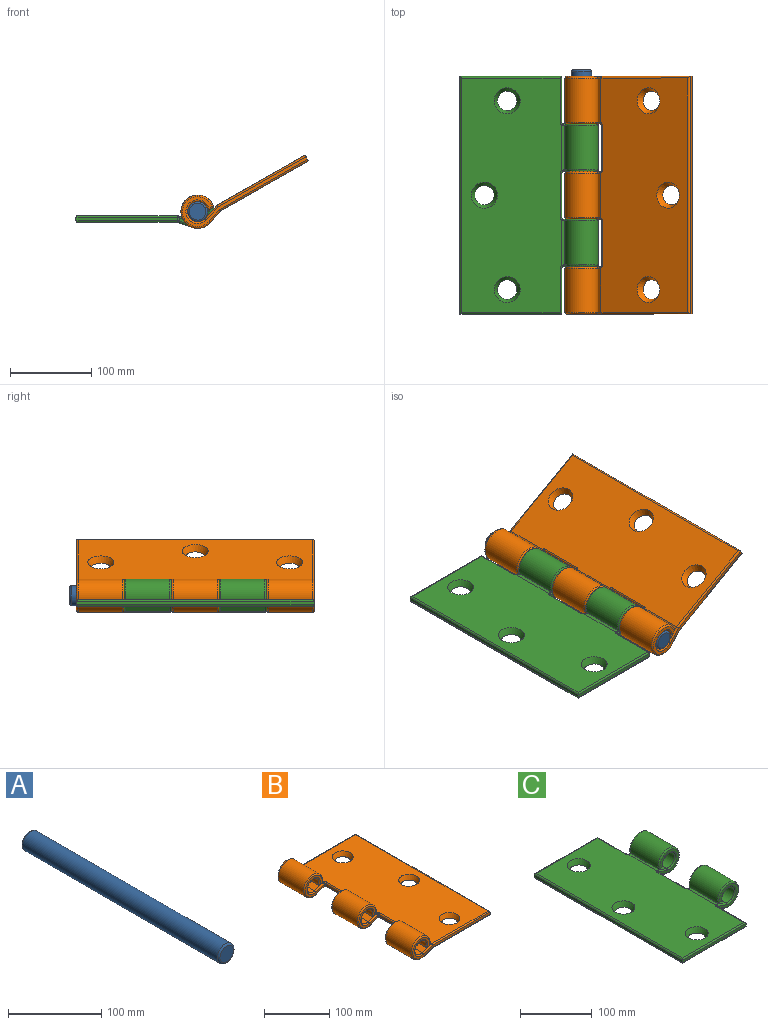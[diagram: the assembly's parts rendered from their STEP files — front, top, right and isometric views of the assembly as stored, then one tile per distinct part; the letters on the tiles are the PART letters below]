
ASSEMBLY  parts=3 mates=2
PART A: 5 faces, bbox 26.5x300x26.5 mm
  f0: cylinder r=12.25mm len=296mm, axis (0,-1,0), area 22782.8mm2, adj f3,f4
  f1: plane 20.5x20.5mm, normal (0,1,0), area 330.1mm2, adj f4
  f2: plane 20.5x20.5mm, normal (0,-1,0), area 330.1mm2, adj f3
  f3: torus R=10.25mm, axis (0,-1,0), area 227.5mm2, adj f0,f2
  f4: torus R=10.25mm, axis (0,-1,0), area 227.5mm2, adj f0,f1
PART B: 89 faces, bbox 171.7x292x44.4 mm
  f0: plane 55.3x20.54mm, normal (-0.32,0,0.95), area 1179mm2, adj f8,f11,f42,f44,f46,f80
  f1: plane 56.21x20.54mm, normal (-0.32,0,0.95), area 1179.8mm2, adj f9,f11,f50,f51,f52,f62,f64,f66
  f2: plane 54.63x17.59mm, normal (0.34,0,-0.94), area 1016.4mm2, adj f4,f13,f33,f34,f73
  f3: plane 54.85x17.59mm, normal (0.34,0,-0.94), area 1016.5mm2, adj f5,f13,f41,f43,f53,f54
  f4: cylinder r=20.5mm len=54.4mm, axis (0,1,0), area 5913.6mm2, adj f2,f6,f36,f74
  f5: cylinder r=20.5mm len=54.4mm, axis (0,1,0), area 5913.6mm2, adj f3,f7,f45,f56
  f6: plane 54.4x8.42mm, normal (0,0,-1), area 458.3mm2, adj f4,f8,f38,f76
  f7: plane 54.4x8.42mm, normal (0,0,-1), area 458.3mm2, adj f5,f9,f47,f58
  f8: cylinder r=12.5mm len=54.4mm, axis (0,1,0), area 3703.3mm2, adj f0,f6,f40,f78
  f9: cylinder r=12.5mm len=54.4mm, axis (0,1,0), area 3703.3mm2, adj f1,f7,f49,f60
  f10: plane 55.3x20.54mm, normal (-0.32,0,0.95), area 1179mm2, adj f11,f17,f70,f71,f72,f88
  f11: plane 288x123mm, normal (0,0,1), area 32774mm2, adj f0,f1,f10,f20,f21,f22,f46,f48
  f12: plane 292x4mm, normal (1,0,0), area 1168mm2, adj f18,f19,f77,f84
  f13: plane 288x123.06mm, normal (0,0,-1), area 33829.6mm2, adj f2,f3,f14,f20,f21,f22,f33,f35
  f14: plane 54.63x17.59mm, normal (0.34,0,-0.94), area 1016.4mm2, adj f13,f15,f61,f63,f81
  f15: cylinder r=20.5mm len=54.4mm, axis (0,1,0), area 5913.6mm2, adj f14,f16,f65,f83
  f16: plane 54.4x8.42mm, normal (0,0,-1), area 458.3mm2, adj f15,f17,f67,f85
  f17: cylinder r=12.5mm len=54.4mm, axis (0,1,0), area 3703.3mm2, adj f10,f16,f69,f87
  f18: plane 168x37mm, normal (0,-1,0), area 921.5mm2, adj f12,f79,f81,f83,f85,f86,f87,f88
  f19: plane 168x37mm, normal (0,1,0), area 921.5mm2, adj f12,f73,f74,f75,f76,f78,f80,f82
  f20: cone r=12mm half-angle=26.6deg, axis (0,0,1), area 786.8mm2, adj f11,f13
  f21: cone r=12mm half-angle=26.6deg, axis (0,0,1), area 786.8mm2, adj f11,f13
  f22: cone r=12mm half-angle=26.6deg, axis (0,0,1), area 786.8mm2, adj f11,f13
  f23: plane 54.4x4mm, normal (-1,0,0), area 217.6mm2, adj f29,f30,f57,f68
  f24: plane 41x37mm, normal (0,1,0), area 413.9mm2, adj f29,f63,f65,f67,f69,f71
  f25: plane 41x37mm, normal (0,-1,0), area 413.9mm2, adj f30,f54,f56,f58,f60,f62
  f26: plane 54.4x4mm, normal (-1,0,0), area 217.6mm2, adj f31,f32,f37,f48
  f27: plane 41x37mm, normal (0,1,0), area 413.9mm2, adj f31,f43,f45,f47,f49,f51
  f28: plane 41x37mm, normal (0,-1,0), area 413.9mm2, adj f32,f34,f36,f38,f40,f42
  f29: cylinder r=2mm len=4.59mm, axis (0,0,-1), area 12.3mm2, adj f23,f24,f59,f61,f70,f72
  f30: cylinder r=2mm len=4.59mm, axis (0,0,1), area 12.3mm2, adj f23,f25,f53,f55,f64,f66
  f31: cylinder r=2mm len=4.59mm, axis (0,0,-1), area 12.3mm2, adj f26,f27,f39,f41,f50,f52
  f32: cylinder r=2mm len=4.59mm, axis (0,0,1), area 12.3mm2, adj f26,f28,f33,f35,f44,f46
  f33: bspline ~2.47x2.33mm, area 3.5mm2, adj f2,f13,f32,f34,f35
  f34: cylinder r=2mm len=16.94mm, axis (-0.94,0,-0.34), area 54.3mm2, adj f2,f28,f33,f36
  f35: torus R=4mm, axis (0,0,-1), area 9.2mm2, adj f13,f32,f33,f37
  f36: torus R=18.5mm, axis (0,-1,0), area 326.9mm2, adj f4,f28,f34,f38
  f37: cylinder r=2mm len=54.4mm, axis (0,1,0), area 170.9mm2, adj f13,f26,f35,f39
  f38: cylinder r=2mm len=8.42mm, axis (-1,0,0), area 19.6mm2, adj f6,f28,f36,f40
  f39: torus R=4mm, axis (0,0,-1), area 9.2mm2, adj f13,f31,f37,f41
  f40: torus R=14.5mm, axis (0,-1,0), area 222mm2, adj f8,f28,f38,f42
  f41: bspline ~2.47x2.33mm, area 3.5mm2, adj f3,f13,f31,f39,f43
  f42: cylinder r=2mm len=18.54mm, axis (0.95,0,0.32), area 59.3mm2, adj f0,f28,f40,f44
  f43: cylinder r=2mm len=16.94mm, axis (0.94,0,0.34), area 54.3mm2, adj f3,f27,f41,f45
  f44: bspline ~2.75x2.54mm, area 6mm2, adj f0,f32,f42,f46
  f45: torus R=18.5mm, axis (0,-1,0), area 326.9mm2, adj f5,f27,f43,f47
  f46: torus R=4mm, axis (0,0,-1), area 8.7mm2, adj f0,f11,f32,f44,f48
  f47: cylinder r=2mm len=8.42mm, axis (1,0,0), area 19.6mm2, adj f7,f27,f45,f49
  f48: cylinder r=2mm len=54.4mm, axis (0,-1,0), area 170.9mm2, adj f11,f26,f46,f50
  f49: torus R=14.5mm, axis (0,-1,0), area 222mm2, adj f9,f27,f47,f51
  f50: torus R=4mm, axis (0,0,-1), area 8.7mm2, adj f1,f11,f31,f48,f52
  f51: cylinder r=2mm len=18.54mm, axis (-0.95,0,-0.32), area 59.3mm2, adj f1,f27,f49,f52
  f52: bspline ~2.75x2.54mm, area 6mm2, adj f1,f31,f50,f51
  f53: bspline ~2.47x2.33mm, area 3.5mm2, adj f3,f13,f30,f54,f55
  f54: cylinder r=2mm len=16.94mm, axis (-0.94,0,-0.34), area 54.3mm2, adj f3,f25,f53,f56
  f55: torus R=4mm, axis (0,0,-1), area 9.2mm2, adj f13,f30,f53,f57
  f56: torus R=18.5mm, axis (0,-1,0), area 326.9mm2, adj f5,f25,f54,f58
  f57: cylinder r=2mm len=54.4mm, axis (0,1,0), area 170.9mm2, adj f13,f23,f55,f59
  f58: cylinder r=2mm len=8.42mm, axis (-1,0,0), area 19.6mm2, adj f7,f25,f56,f60
  f59: torus R=4mm, axis (0,0,-1), area 9.2mm2, adj f13,f29,f57,f61
  f60: torus R=14.5mm, axis (0,-1,0), area 222mm2, adj f9,f25,f58,f62
  f61: bspline ~2.47x2.33mm, area 3.5mm2, adj f13,f14,f29,f59,f63
  f62: cylinder r=2mm len=18.54mm, axis (0.95,0,0.32), area 59.3mm2, adj f1,f25,f60,f64
  f63: cylinder r=2mm len=16.94mm, axis (0.94,0,0.34), area 54.3mm2, adj f14,f24,f61,f65
  f64: bspline ~3.65x3.11mm, area 6mm2, adj f1,f30,f62,f66
  f65: torus R=18.5mm, axis (0,-1,0), area 326.9mm2, adj f15,f24,f63,f67
  f66: torus R=4mm, axis (0,0,-1), area 8.7mm2, adj f1,f11,f30,f64,f68
  f67: cylinder r=2mm len=8.42mm, axis (1,0,0), area 19.6mm2, adj f16,f24,f65,f69
  f68: cylinder r=2mm len=54.4mm, axis (0,-1,0), area 170.9mm2, adj f11,f23,f66,f70
  f69: torus R=14.5mm, axis (0,-1,0), area 222mm2, adj f17,f24,f67,f71
  f70: torus R=4mm, axis (0,0,-1), area 8.7mm2, adj f10,f11,f29,f68,f72
  f71: cylinder r=2mm len=18.54mm, axis (-0.95,0,-0.32), area 59.3mm2, adj f10,f24,f69,f72
  f72: bspline ~3.65x3.11mm, area 6mm2, adj f10,f29,f70,f71
  f73: cylinder r=2mm len=18.59mm, axis (-0.94,0,-0.34), area 59.2mm2, adj f2,f19,f74,f75
  f74: torus R=18.5mm, axis (0,-1,0), area 326.9mm2, adj f4,f19,f73,f76
  f75: cylinder r=2mm len=125.35mm, axis (-1,0,0), area 390.1mm2, adj f13,f19,f73,f77
  f76: cylinder r=2mm len=8.42mm, axis (-1,0,0), area 19.6mm2, adj f6,f19,f74,f78
  f77: cylinder r=2mm len=292mm, axis (0,-1,0), area 911.1mm2, adj f12,f13,f75,f79
  f78: torus R=14.5mm, axis (0,-1,0), area 222mm2, adj f8,f19,f76,f80
  f79: cylinder r=2mm len=125.35mm, axis (1,0,0), area 390.1mm2, adj f13,f18,f77,f81
  f80: cylinder r=2mm len=21.18mm, axis (0.95,0,0.32), area 67.5mm2, adj f0,f19,f78,f82
  f81: cylinder r=2mm len=18.59mm, axis (0.94,0,0.34), area 59.2mm2, adj f14,f18,f79,f83
  f82: cylinder r=2mm len=125mm, axis (1,0,0), area 389mm2, adj f11,f19,f80,f84
  f83: torus R=18.5mm, axis (0,-1,0), area 326.9mm2, adj f15,f18,f81,f85
  f84: cylinder r=2mm len=292mm, axis (0,1,0), area 911.1mm2, adj f11,f12,f82,f86
  f85: cylinder r=2mm len=8.42mm, axis (1,0,0), area 19.6mm2, adj f16,f18,f83,f87
  f86: cylinder r=2mm len=125mm, axis (-1,0,0), area 389mm2, adj f11,f18,f84,f88
  f87: torus R=14.5mm, axis (0,-1,0), area 222mm2, adj f17,f18,f85,f88
  f88: cylinder r=2mm len=21.18mm, axis (-0.95,0,-0.32), area 67.5mm2, adj f10,f18,f86,f87
PART C: 77 faces, bbox 171.7x292x44.4 mm
  f0: plane 56.21x20.54mm, normal (0.32,0,0.95), area 1179.8mm2, adj f8,f10,f29,f30,f31,f74,f75,f76
  f1: plane 56.21x20.54mm, normal (0.32,0,0.95), area 1179.8mm2, adj f9,f10,f35,f37,f39,f59,f61,f63
  f2: plane 54.85x17.59mm, normal (-0.34,0,-0.94), area 1016.5mm2, adj f4,f12,f38,f40,f64,f66
  f3: plane 54.85x17.59mm, normal (-0.34,0,-0.94), area 1016.5mm2, adj f5,f12,f47,f48,f49,f51
  f4: cylinder r=20.5mm len=54.4mm, axis (0,1,0), area 5913.6mm2, adj f2,f6,f36,f68
  f5: cylinder r=20.5mm len=54.4mm, axis (0,1,0), area 5913.6mm2, adj f3,f7,f45,f53
  f6: plane 54.4x8.42mm, normal (0,0,-1), area 458.3mm2, adj f4,f8,f34,f70
  f7: plane 54.4x8.42mm, normal (0,0,-1), area 458.3mm2, adj f5,f9,f43,f55
  f8: cylinder r=12.5mm len=54.4mm, axis (0,1,0), area 3703.3mm2, adj f0,f6,f32,f72
  f9: cylinder r=12.5mm len=54.4mm, axis (0,1,0), area 3703.3mm2, adj f1,f7,f41,f57
  f10: plane 288x123mm, normal (0,0,1), area 32665.2mm2, adj f0,f1,f15,f16,f17,f31,f33,f35
  f11: plane 292x4mm, normal (-1,0,0), area 1168mm2, adj f13,f14,f56,f69
  f12: plane 288x123.06mm, normal (0,0,-1), area 33720.8mm2, adj f2,f3,f15,f16,f17,f40,f42,f44
  f13: plane 125x4mm, normal (0,-1,0), area 500mm2, adj f11,f18,f54,f67
  f14: plane 125x4mm, normal (0,1,0), area 500mm2, adj f11,f23,f58,f71
  f15: cone r=12mm half-angle=26.6deg, axis (0,0,1), area 786.8mm2, adj f10,f12
  f16: cone r=12mm half-angle=26.6deg, axis (0,0,1), area 786.8mm2, adj f10,f12
  f17: cone r=12mm half-angle=26.6deg, axis (0,0,1), area 786.8mm2, adj f10,f12
  f18: plane 56.4x4mm, normal (1,0,0), area 225.6mm2, adj f13,f25,f52,f65
  f19: plane 41x37mm, normal (0,-1,0), area 413.9mm2, adj f25,f51,f53,f55,f57,f59
  f20: plane 54.4x4mm, normal (1,0,0), area 217.6mm2, adj f26,f27,f33,f44
  f21: plane 41x37mm, normal (0,-1,0), area 413.9mm2, adj f26,f30,f32,f34,f36,f38
  f22: plane 41x37mm, normal (0,1,0), area 413.9mm2, adj f27,f39,f41,f43,f45,f47
  f23: plane 56.4x4mm, normal (1,0,0), area 225.6mm2, adj f14,f28,f60,f73
  f24: plane 41x37mm, normal (0,1,0), area 413.9mm2, adj f28,f66,f68,f70,f72,f74
  f25: cylinder r=2mm len=4.59mm, axis (0,0,1), area 12.3mm2, adj f18,f19,f49,f50,f61,f63
  f26: cylinder r=2mm len=4.59mm, axis (0,0,1), area 12.3mm2, adj f20,f21,f29,f31,f40,f42
  f27: cylinder r=2mm len=4.59mm, axis (0,0,-1), area 12.3mm2, adj f20,f22,f35,f37,f46,f48
  f28: cylinder r=2mm len=4.59mm, axis (0,0,-1), area 12.3mm2, adj f23,f24,f62,f64,f75,f76
  f29: bspline ~2.75x2.54mm, area 6mm2, adj f0,f26,f30,f31
  f30: cylinder r=2mm len=18.54mm, axis (0.95,0,-0.32), area 59.3mm2, adj f0,f21,f29,f32
  f31: torus R=4mm, axis (0,0,-1), area 8.7mm2, adj f0,f10,f26,f29,f33
  f32: torus R=14.5mm, axis (0,1,0), area 222mm2, adj f8,f21,f30,f34
  f33: cylinder r=2mm len=54.4mm, axis (0,1,0), area 170.9mm2, adj f10,f20,f31,f35
  f34: cylinder r=2mm len=8.42mm, axis (-1,0,0), area 19.6mm2, adj f6,f21,f32,f36
  f35: torus R=4mm, axis (0,0,-1), area 8.7mm2, adj f1,f10,f27,f33,f37
  f36: torus R=18.5mm, axis (0,1,0), area 326.9mm2, adj f4,f21,f34,f38
  f37: bspline ~2.75x2.54mm, area 6mm2, adj f1,f27,f35,f39
  f38: cylinder r=2mm len=16.94mm, axis (-0.94,0,0.34), area 54.3mm2, adj f2,f21,f36,f40
  f39: cylinder r=2mm len=18.54mm, axis (-0.95,0,0.32), area 59.3mm2, adj f1,f22,f37,f41
  f40: bspline ~2.47x2.33mm, area 3.5mm2, adj f2,f12,f26,f38,f42
  f41: torus R=14.5mm, axis (0,1,0), area 222mm2, adj f9,f22,f39,f43
  f42: torus R=4mm, axis (0,0,-1), area 9.2mm2, adj f12,f26,f40,f44
  f43: cylinder r=2mm len=8.42mm, axis (1,0,0), area 19.6mm2, adj f7,f22,f41,f45
  f44: cylinder r=2mm len=54.4mm, axis (0,-1,0), area 170.9mm2, adj f12,f20,f42,f46
  f45: torus R=18.5mm, axis (0,1,0), area 326.9mm2, adj f5,f22,f43,f47
  f46: torus R=4mm, axis (0,0,-1), area 9.2mm2, adj f12,f27,f44,f48
  f47: cylinder r=2mm len=16.94mm, axis (0.94,0,-0.34), area 54.3mm2, adj f3,f22,f45,f48
  f48: bspline ~2.47x2.33mm, area 3.5mm2, adj f3,f12,f27,f46,f47
  f49: bspline ~2.47x2.33mm, area 3.5mm2, adj f3,f12,f25,f50,f51
  f50: torus R=4mm, axis (0,0,-1), area 9.2mm2, adj f12,f25,f49,f52
  f51: cylinder r=2mm len=16.94mm, axis (-0.94,0,0.34), area 54.3mm2, adj f3,f19,f49,f53
  f52: cylinder r=2mm len=56.4mm, axis (0,-1,0), area 174mm2, adj f12,f18,f50,f54
  f53: torus R=18.5mm, axis (0,1,0), area 326.9mm2, adj f5,f19,f51,f55
  f54: cylinder r=2mm len=125mm, axis (-1,0,0), area 386.4mm2, adj f12,f13,f52,f56
  f55: cylinder r=2mm len=8.42mm, axis (-1,0,0), area 19.6mm2, adj f7,f19,f53,f57
  f56: cylinder r=2mm len=292mm, axis (0,-1,0), area 911.1mm2, adj f11,f12,f54,f58
  f57: torus R=14.5mm, axis (0,1,0), area 222mm2, adj f9,f19,f55,f59
  f58: cylinder r=2mm len=125mm, axis (1,0,0), area 386.4mm2, adj f12,f14,f56,f60
  f59: cylinder r=2mm len=18.54mm, axis (0.95,0,-0.32), area 59.3mm2, adj f1,f19,f57,f61
  f60: cylinder r=2mm len=56.4mm, axis (0,1,0), area 174mm2, adj f12,f23,f58,f62
  f61: bspline ~3.65x3.11mm, area 6mm2, adj f1,f25,f59,f63
  f62: torus R=4mm, axis (0,0,-1), area 9.2mm2, adj f12,f28,f60,f64
  f63: torus R=4mm, axis (0,0,-1), area 8.7mm2, adj f1,f10,f25,f61,f65
  f64: bspline ~2.47x2.33mm, area 3.5mm2, adj f2,f12,f28,f62,f66
  f65: cylinder r=2mm len=56.4mm, axis (0,1,0), area 174mm2, adj f10,f18,f63,f67
  f66: cylinder r=2mm len=16.94mm, axis (0.94,0,-0.34), area 54.3mm2, adj f2,f24,f64,f68
  f67: cylinder r=2mm len=125mm, axis (1,0,0), area 386.4mm2, adj f10,f13,f65,f69
  f68: torus R=18.5mm, axis (0,1,0), area 326.9mm2, adj f4,f24,f66,f70
  f69: cylinder r=2mm len=292mm, axis (0,1,0), area 911.1mm2, adj f10,f11,f67,f71
  f70: cylinder r=2mm len=8.42mm, axis (1,0,0), area 19.6mm2, adj f6,f24,f68,f72
  f71: cylinder r=2mm len=125mm, axis (-1,0,0), area 386.4mm2, adj f10,f14,f69,f73
  f72: torus R=14.5mm, axis (0,1,0), area 222mm2, adj f8,f24,f70,f74
  f73: cylinder r=2mm len=56.4mm, axis (0,1,0), area 174mm2, adj f10,f23,f71,f75
  f74: cylinder r=2mm len=18.54mm, axis (-0.95,0,0.32), area 59.3mm2, adj f0,f24,f72,f76
  f75: torus R=4mm, axis (0,0,-1), area 8.7mm2, adj f0,f10,f28,f73,f76
  f76: bspline ~2.75x2.54mm, area 6mm2, adj f0,f28,f74,f75
PLACE A rot(axis=(0,1,0),144.6deg) t=(-119.03,51.71,-23.3)mm
PLACE B rot(axis=(0,-1,0),29.7deg) t=(-154.94,43.71,-58.02)mm
PLACE C t=(-160.62,43.71,-46.56)mm fixed
MATE revolute C.f4 <-> B.f36  axis (0,1,0) through (-136.12,-14.69,-41.56)mm
MATE revolute B.f36 <-> A.f0  axis (0,1,0) through (-136.12,-246.29,-41.56)mm
